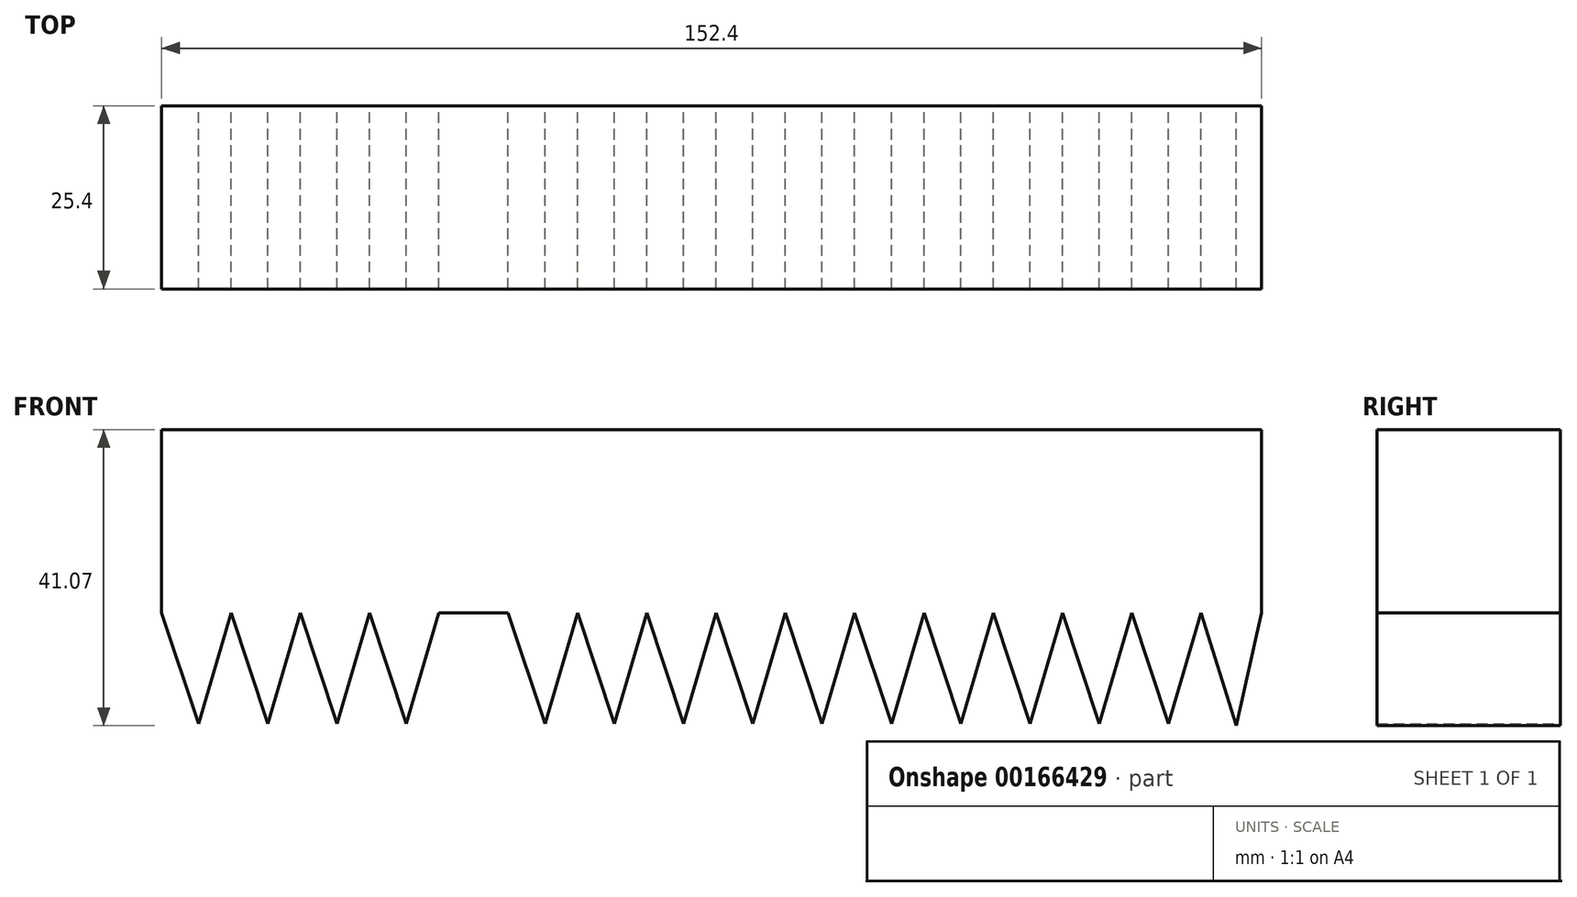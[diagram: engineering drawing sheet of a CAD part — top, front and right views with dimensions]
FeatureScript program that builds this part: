
annotation { "Feature Type Name" : "Feature", "Feature Type Description" : "" }
export const myFeature = defineFeature(function(context is Context, id is Id, definition is map)
    precondition{}
    {
        {
            var Q0;
            Q0=qCreatedBy(makeId("Front.planeOp"),FACE);
            var sketch = newSketch(context, id + "F0", { "sketchPlane" : qUnion([Q0])});
            skLineSegment(sketch, "E0.bottom", {"start": v(76.2, 12.7) * mm, "end": v(-76.2, 12.7) * mm});
            skLineSegment(sketch, "E0.top", {"start": v(76.2, -12.7) * mm, "end": v(-76.2, -12.7) * mm});
            skLineSegment(sketch, "E0.left", {"start": v(76.2, 12.7) * mm, "end": v(76.2, -12.7) * mm});
            skLineSegment(sketch, "E0.right", {"start": v(-76.2, 12.7) * mm, "end": v(-76.2, -12.7) * mm});
            skPoint(sketch, "E0.middle", {"position": v(0, 0) * mm});
            skPoint(sketch, "E1", {"position": v(-76.2, -12.7) * mm});
            skPoint(sketch, "E2", {"position": v(-66.6, -12.7) * mm});
            skPoint(sketch, "E3", {"position": v(-71.1, -28.1) * mm});
            skLineSegment(sketch, "E4", {"start": v(-76.2, -12.7) * mm, "end": v(-71.1, -28.1) * mm});
            skLineSegment(sketch, "E5", {"start": v(-66.6, -12.7) * mm, "end": v(-71.1, -28.1) * mm});
            skLineSegment(sketch, "E6", {"start": v(-76.2, -12.7) * mm, "end": v(-66.6, -12.7) * mm});
            skPoint(sketch, "E7.1.0.0", {"position": v(-61.5, -28.1) * mm});
            skPoint(sketch, "E7.2.0.0", {"position": v(-51.9, -28.1) * mm});
            skPoint(sketch, "E7.3.0.0", {"position": v(-42.3, -28.1) * mm});
            skPoint(sketch, "E7.4.0.0", {"position": v(-32.7, -28.1) * mm});
            skPoint(sketch, "E7.5.0.0", {"position": v(-23.1, -28.1) * mm});
            skPoint(sketch, "E7.6.0.0", {"position": v(-13.5, -28.1) * mm});
            skPoint(sketch, "E7.7.0.0", {"position": v(-3.89, -28.1) * mm});
            skPoint(sketch, "E7.8.0.0", {"position": v(5.71, -28.1) * mm});
            skPoint(sketch, "E7.9.0.0", {"position": v(15.31, -28.1) * mm});
            skPoint(sketch, "E7.10.0.0", {"position": v(24.91, -28.1) * mm});
            skPoint(sketch, "E7.11.0.0", {"position": v(34.51, -28.1) * mm});
            skPoint(sketch, "E7.12.0.0", {"position": v(44.12, -28.1) * mm});
            skPoint(sketch, "E7.13.0.0", {"position": v(53.72, -28.1) * mm});
            skPoint(sketch, "E7.14.0.0", {"position": v(63.32, -28.1) * mm});
            skLineSegment(sketch, "E7.direction1", {"start": v(-71.1, -28.1) * mm, "end": v(-61.5, -28.1) * mm, "construction": true});
            skPoint(sketch, "E8.1.0.0", {"position": v(-57, -12.7) * mm});
            skPoint(sketch, "E8.2.0.0", {"position": v(-47.4, -12.7) * mm});
            skPoint(sketch, "E8.3.0.0", {"position": v(-37.79, -12.7) * mm});
            skPoint(sketch, "E8.4.0.0", {"position": v(-28.19, -12.7) * mm});
            skPoint(sketch, "E8.5.0.0", {"position": v(-18.59, -12.7) * mm});
            skPoint(sketch, "E8.6.0.0", {"position": v(-8.99, -12.7) * mm});
            skPoint(sketch, "E8.7.0.0", {"position": v(0.62, -12.7) * mm});
            skPoint(sketch, "E8.8.0.0", {"position": v(10.22, -12.7) * mm});
            skPoint(sketch, "E8.9.0.0", {"position": v(19.82, -12.7) * mm});
            skPoint(sketch, "E8.10.0.0", {"position": v(29.42, -12.7) * mm});
            skPoint(sketch, "E8.11.0.0", {"position": v(39.02, -12.7) * mm});
            skPoint(sketch, "E8.12.0.0", {"position": v(48.62, -12.7) * mm});
            skPoint(sketch, "E8.13.0.0", {"position": v(58.22, -12.7) * mm});
            skPoint(sketch, "E8.14.0.0", {"position": v(67.82, -12.7) * mm});
            skLineSegment(sketch, "E8.direction1", {"start": v(-66.6, -12.7) * mm, "end": v(-57, -12.7) * mm, "construction": true});
            skLineSegment(sketch, "E9", {"start": v(-66.6, -12.7) * mm, "end": v(-61.5, -28.1) * mm});
            skLineSegment(sketch, "E10", {"start": v(-57, -12.7) * mm, "end": v(-61.5, -28.1) * mm});
            skLineSegment(sketch, "E11", {"start": v(-51.9, -28.1) * mm, "end": v(-57, -12.7) * mm});
            skLineSegment(sketch, "E12", {"start": v(-47.4, -12.7) * mm, "end": v(-51.9, -28.1) * mm});
            skLineSegment(sketch, "E13", {"start": v(-47.4, -12.7) * mm, "end": v(-42.3, -28.1) * mm});
            skLineSegment(sketch, "E14", {"start": v(-37.79, -12.7) * mm, "end": v(-42.3, -28.1) * mm});
            skLineSegment(sketch, "E15", {"start": v(-37.8, -13.02) * mm, "end": v(-32.7, -28.1) * mm});
            skLineSegment(sketch, "E16", {"start": v(-28.19, -12.7) * mm, "end": v(-23.1, -28.1) * mm});
            skLineSegment(sketch, "E17", {"start": v(-18.59, -12.7) * mm, "end": v(-23.1, -28.1) * mm});
            skLineSegment(sketch, "E18", {"start": v(-18.59, -12.7) * mm, "end": v(-13.5, -28.1) * mm});
            skLineSegment(sketch, "E19", {"start": v(-8.99, -12.7) * mm, "end": v(-13.5, -28.1) * mm});
            skLineSegment(sketch, "E20", {"start": v(-8.99, -12.7) * mm, "end": v(-3.89, -28.1) * mm});
            skLineSegment(sketch, "E21", {"start": v(0.62, -12.7) * mm, "end": v(-3.89, -28.1) * mm});
            skLineSegment(sketch, "E22", {"start": v(0.62, -12.7) * mm, "end": v(5.71, -28.1) * mm});
            skLineSegment(sketch, "E23", {"start": v(10.22, -12.7) * mm, "end": v(5.71, -28.1) * mm});
            skLineSegment(sketch, "E24", {"start": v(10.22, -12.7) * mm, "end": v(15.31, -28.1) * mm});
            skLineSegment(sketch, "E25", {"start": v(19.82, -12.7) * mm, "end": v(15.31, -28.1) * mm});
            skLineSegment(sketch, "E26", {"start": v(19.82, -12.7) * mm, "end": v(24.91, -28.1) * mm});
            skLineSegment(sketch, "E27", {"start": v(29.42, -12.7) * mm, "end": v(24.91, -28.1) * mm});
            skLineSegment(sketch, "E28", {"start": v(29.42, -12.7) * mm, "end": v(34.51, -28.1) * mm});
            skLineSegment(sketch, "E29", {"start": v(39.02, -12.7) * mm, "end": v(34.51, -28.1) * mm});
            skLineSegment(sketch, "E30", {"start": v(39.02, -12.7) * mm, "end": v(44.12, -28.1) * mm});
            skLineSegment(sketch, "E31", {"start": v(48.62, -12.7) * mm, "end": v(44.12, -28.1) * mm});
            skLineSegment(sketch, "E32", {"start": v(48.62, -12.7) * mm, "end": v(53.72, -28.1) * mm});
            skLineSegment(sketch, "E33", {"start": v(58.22, -12.7) * mm, "end": v(53.72, -28.1) * mm});
            skLineSegment(sketch, "E34", {"start": v(58.22, -12.7) * mm, "end": v(63.32, -28.1) * mm});
            skLineSegment(sketch, "E35", {"start": v(67.82, -12.7) * mm, "end": v(63.32, -28.1) * mm});
            skPoint(sketch, "E36", {"position": v(76.2, -12.7) * mm});
            skPoint(sketch, "E37", {"position": v(72.72, -28.37) * mm});
            skLineSegment(sketch, "E38", {"start": v(67.82, -12.7) * mm, "end": v(72.72, -28.37) * mm});
            skLineSegment(sketch, "E39", {"start": v(76.2, -12.7) * mm, "end": v(72.72, -28.37) * mm});
            skLineSegment(sketch, "E40", {"start": v(-28.19, -12.7) * mm, "end": v(-32.7, -28.1) * mm});
            skLineSegment(sketch, "E41", {"start": v(-37.79, -12.7) * mm, "end": v(-28.19, -12.7) * mm});
            skLineSegment(sketch, "E42", {"start": v(-37.79, -12.7) * mm, "end": v(-32.7, -28.1) * mm});
            skLineSegment(sketch, "E43", {"start": v(-76.2, -12.7) * mm, "end": v(76.2, -12.7) * mm});
            skSolve(sketch);
        }
        {
            var Q0;
            Q0=makeQuery(id+"F0.imprint","IMPRINT",FACE,{"disambiguationData":[TD([[makeQuery(id+"F0.imprint","IMPRINT",EDGE,{"derivedFrom":sQuery(id+"F0.wireOp",EDGE,"E0.bottom")}),1.0]])]});
            var Q1;
            Q1=makeQuery(id+"F0.imprint","IMPRINT",FACE,{"disambiguationData":[TD([[makeQuery(id+"F0.imprint","IMPRINT",EDGE,{"derivedFrom":sQuery(id+"F0.wireOp",EDGE,"E4")}),1.0]])]});
            var Q2;
            {var subQ0=sQuery(id+"F0.wireOp",EDGE,"E9");Q2=makeQuery(id+"F0.imprint","IMPRINT",FACE,{"disambiguationData":[TD([[makeQuery(id+"F0.imprint","IMPRINT",EDGE,{"derivedFrom":subQ0}),1.0]])]});}
            var Q3;
            {var subQ0=sQuery(id+"F0.wireOp",EDGE,"E11");Q3=makeQuery(id+"F0.imprint","IMPRINT",FACE,{"disambiguationData":[TD([[makeQuery(id+"F0.imprint","IMPRINT",EDGE,{"derivedFrom":subQ0}),-1.0]])]});}
            var Q4;
            {var subQ0=sQuery(id+"F0.wireOp",EDGE,"E13");Q4=makeQuery(id+"F0.imprint","IMPRINT",FACE,{"disambiguationData":[TD([[makeQuery(id+"F0.imprint","IMPRINT",EDGE,{"derivedFrom":subQ0}),1.0]])]});}
            var Q5;
            {var subQ0=sQuery(id+"F0.wireOp",EDGE,"E16");Q5=makeQuery(id+"F0.imprint","IMPRINT",FACE,{"disambiguationData":[TD([[makeQuery(id+"F0.imprint","IMPRINT",EDGE,{"derivedFrom":subQ0}),1.0]])]});}
            var Q6;
            {var subQ0=sQuery(id+"F0.wireOp",EDGE,"E18");Q6=makeQuery(id+"F0.imprint","IMPRINT",FACE,{"disambiguationData":[TD([[makeQuery(id+"F0.imprint","IMPRINT",EDGE,{"derivedFrom":subQ0}),1.0]])]});}
            var Q7;
            {var subQ0=sQuery(id+"F0.wireOp",EDGE,"E20");Q7=makeQuery(id+"F0.imprint","IMPRINT",FACE,{"disambiguationData":[TD([[makeQuery(id+"F0.imprint","IMPRINT",EDGE,{"derivedFrom":subQ0}),1.0]])]});}
            var Q8;
            {var subQ0=sQuery(id+"F0.wireOp",EDGE,"E22");Q8=makeQuery(id+"F0.imprint","IMPRINT",FACE,{"disambiguationData":[TD([[makeQuery(id+"F0.imprint","IMPRINT",EDGE,{"derivedFrom":subQ0}),1.0]])]});}
            var Q9;
            {var subQ0=sQuery(id+"F0.wireOp",EDGE,"E24");Q9=makeQuery(id+"F0.imprint","IMPRINT",FACE,{"disambiguationData":[TD([[makeQuery(id+"F0.imprint","IMPRINT",EDGE,{"derivedFrom":subQ0}),1.0]])]});}
            var Q10;
            {var subQ0=sQuery(id+"F0.wireOp",EDGE,"E26");Q10=makeQuery(id+"F0.imprint","IMPRINT",FACE,{"disambiguationData":[TD([[makeQuery(id+"F0.imprint","IMPRINT",EDGE,{"derivedFrom":subQ0}),1.0]])]});}
            var Q11;
            {var subQ0=sQuery(id+"F0.wireOp",EDGE,"E28");Q11=makeQuery(id+"F0.imprint","IMPRINT",FACE,{"disambiguationData":[TD([[makeQuery(id+"F0.imprint","IMPRINT",EDGE,{"derivedFrom":subQ0}),1.0]])]});}
            var Q12;
            {var subQ0=sQuery(id+"F0.wireOp",EDGE,"E30");Q12=makeQuery(id+"F0.imprint","IMPRINT",FACE,{"disambiguationData":[TD([[makeQuery(id+"F0.imprint","IMPRINT",EDGE,{"derivedFrom":subQ0}),1.0]])]});}
            var Q13;
            {var subQ0=sQuery(id+"F0.wireOp",EDGE,"E32");Q13=makeQuery(id+"F0.imprint","IMPRINT",FACE,{"disambiguationData":[TD([[makeQuery(id+"F0.imprint","IMPRINT",EDGE,{"derivedFrom":subQ0}),1.0]])]});}
            var Q14;
            {var subQ0=sQuery(id+"F0.wireOp",EDGE,"E34");Q14=makeQuery(id+"F0.imprint","IMPRINT",FACE,{"disambiguationData":[TD([[makeQuery(id+"F0.imprint","IMPRINT",EDGE,{"derivedFrom":subQ0}),1.0]])]});}
            var Q15;
            {var subQ2=sQuery(id+"F0.wireOp",EDGE,"E38");Q15=makeQuery(id+"F0.imprint","IMPRINT",FACE,{"disambiguationData":[TD([[makeQuery(id+"F0.imprint","IMPRINT",EDGE,{"derivedFrom":subQ2}),1.0]])]});}
            extrude(context, id + "F1", {"entities" : qUnion([Q0, Q1, Q2, Q3, Q4, Q5, Q6, Q7, Q8, Q9, Q10, Q11, Q12, Q13, Q14, Q15]), "depth" : 25.4 * mm});
        }
    });
